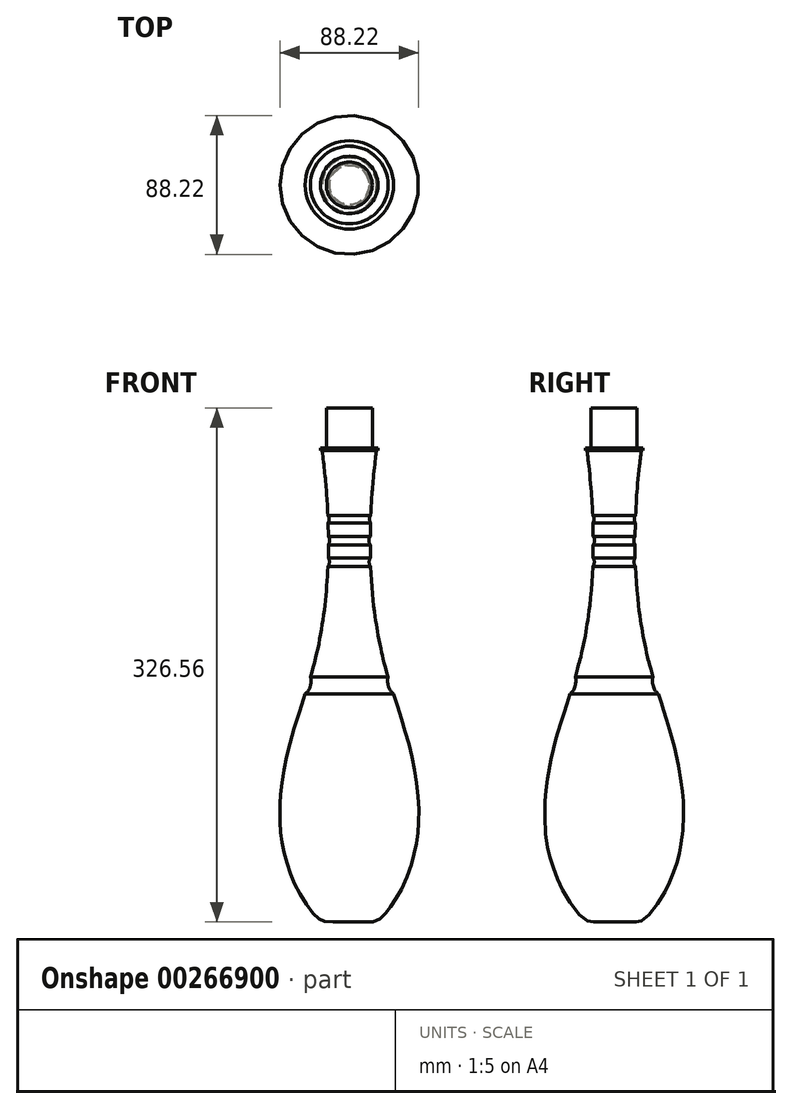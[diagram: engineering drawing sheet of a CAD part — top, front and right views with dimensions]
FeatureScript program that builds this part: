
annotation { "Feature Type Name" : "Feature", "Feature Type Description" : "" }
export const myFeature = defineFeature(function(context is Context, id is Id, definition is map)
    precondition{}
    {
        {
            var Q0;
            Q0=qCreatedBy(makeId("Front.planeOp"),FACE);
            var sketch = newSketch(context, id + "F0", { "sketchPlane" : qUnion([Q0])});
            skLineSegment(sketch, "E0", {"start": v(0, 179.05) * mm, "end": v(0, -124.1) * mm});
            skLineSegment(sketch, "E1", {"start": v(0, -124.1) * mm, "end": v(0, -147.3) * mm});
            skFitSpline(sketch, "E2", {"points": [v(0, -147.3) * mm, v(-16.86, -146.87) * mm, v(-20.87, -144.2) * mm, v(-30.07, -132) * mm, v(-37.1, -117.61) * mm, v(-41.6, -102.73) * mm, v(-43.61, -90.03) * mm, v(-44.11, -77.32) * mm, v(-43.78, -68.3) * mm, v(-41.27, -50.07) * mm, v(-35.25, -25.5) * mm, v(-28.23, -3.26) * mm, v(-28.1, -2.74) * mm], "startDerivative": vector(-310.26, -5.3) * mm, "endDerivative": vector(3.22, 17.89) * mm});
            skFitSpline(sketch, "E3", {"points": [v(-28.1, -2.74) * mm, v(-25.48, 0.54) * mm, v(-24.39, 4.36) * mm, v(-24.3, 6.3) * mm, v(-24.65, 8.24) * mm], "startDerivative": vector(9.9, 10.05) * mm, "endDerivative": vector(-2.07, 9.7) * mm});
            skFitSpline(sketch, "E4", {"points": [v(-24.65, 8.24) * mm, v(-21.63, 19.34) * mm, v(-20.17, 25.53) * mm, v(-18.13, 35.58) * mm, v(-17.04, 42.4) * mm, v(-15.28, 55.15) * mm, v(-13.56, 78.37) * mm], "startDerivative": vector(20, 72.25) * mm, "endDerivative": vector(6.1, 102.62) * mm});
            skFitSpline(sketch, "E5", {"points": [v(-13.56, 78.37) * mm, v(-12.95, 79.4) * mm, v(-12.63, 80.98) * mm, v(-12.78, 82.58) * mm, v(-13.32, 83.9) * mm], "startDerivative": vector(2.94, 4.2) * mm, "endDerivative": vector(-2.55, 5.18) * mm});
            skLineSegment(sketch, "E6", {"start": v(-13.32, 83.9) * mm, "end": v(-13.32, 92.17) * mm});
            skFitSpline(sketch, "E7", {"points": [v(-13.32, 92.17) * mm, v(-12.6, 93.59) * mm, v(-12.47, 95.08) * mm, v(-12.74, 96.42) * mm, v(-13.32, 97.37) * mm], "startDerivative": vector(3.18, 5.15) * mm, "endDerivative": vector(-2.9, 3.96) * mm});
            skLineSegment(sketch, "E8", {"start": v(-13.32, 97.37) * mm, "end": v(-13.49, 106.15) * mm});
            skFitSpline(sketch, "E9", {"points": [v(-13.49, 106.15) * mm, v(-12.92, 107.54) * mm, v(-12.9, 109.27) * mm, v(-13.2, 110.23) * mm, v(-13.6, 110.88) * mm], "startDerivative": vector(2.47, 4.7) * mm, "endDerivative": vector(-2.22, 3.16) * mm});
            skFitSpline(sketch, "E10", {"points": [v(-13.6, 110.88) * mm, v(-14.26, 122.58) * mm, v(-15.08, 132.57) * mm, v(-16.56, 146.34) * mm, v(-17.18, 151.93) * mm], "startDerivative": vector(-2.35, 45.1) * mm, "endDerivative": vector(-2.88, 25.8) * mm});
            skLineSegment(sketch, "E11", {"start": v(-17.18, 151.93) * mm, "end": v(-18.23, 151.93) * mm});
            skLineSegment(sketch, "E12", {"start": v(-18.23, 151.93) * mm, "end": v(-18.23, 153.49) * mm});
            skLineSegment(sketch, "E13", {"start": v(-18.23, 153.49) * mm, "end": v(-14.6, 153.49) * mm});
            skLineSegment(sketch, "E14", {"start": v(-14.6, 153.49) * mm, "end": v(-14.6, 179.1) * mm});
            skLineSegment(sketch, "E15", {"start": v(-14.6, 179.1) * mm, "end": v(0, 179.05) * mm});
            skSolve(sketch);
        }
        {
            var Q0;
            Q0 = qSketchRegion(id + "F0", true);
            var Q1;
            Q1=sQuery(id+"F0.wireOp",EDGE,"E0");
            revolve(context, id + "F1", {"entities" : qUnion([Q0]), "axis" : qUnion([Q1]), "revolveType" : RevolveType.FULL});
        }
    });
